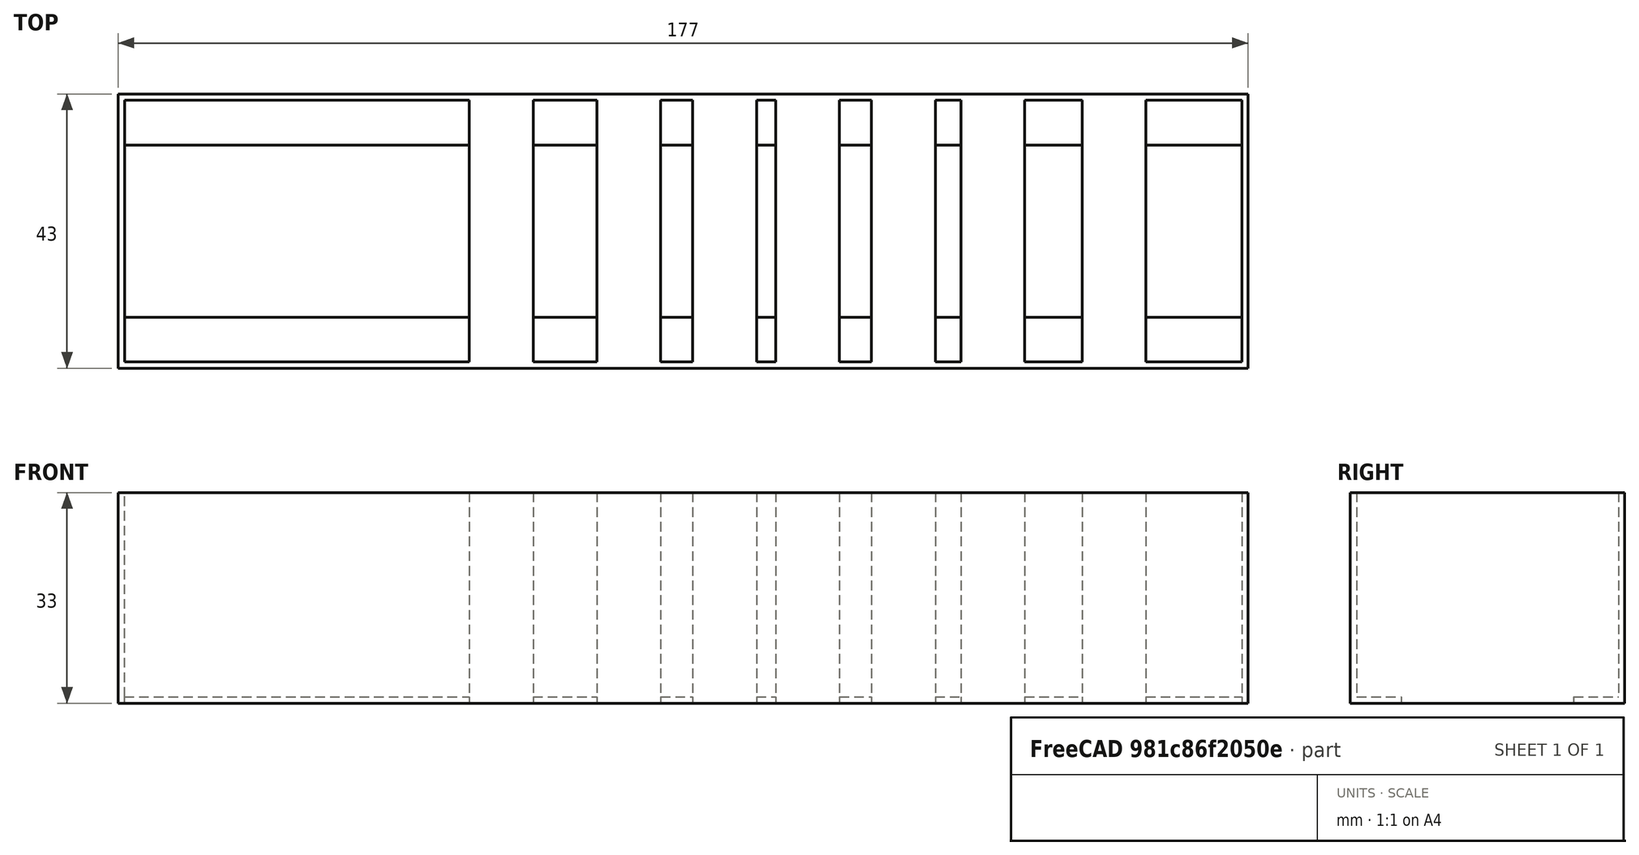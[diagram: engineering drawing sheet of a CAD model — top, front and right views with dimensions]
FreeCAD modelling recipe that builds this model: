
FCSTD DOCUMENT  (FreeCAD 0.18R4 (GitTag))
Label: common
License: All rights reserved
LicenseURL: http://en.wikipedia.org/wiki/All_rights_reserved
objects: Part::Box×13, Part::Cut×2, Part::MultiFuse×2
note: 17 computed .brp shape members not serialized (recipe doc carries the construction recipe); baked Part::Feature solids carry a one-line shape summary decoded from their .brp

FEATURE [Part::Box] Box  label="Cube"
  AttacherType = Attacher::AttachEngine3D
  Height = 33
  Length = 202
  Width = 43
FEATURE [Part::Box] Box001  label="Cube001"
  AttacherType = Attacher::AttachEngine3D
  Height = 33
  Length = 200
  Placement = pos=(1,1,0) rot=(0,0,1;0rad)
  Width = 41
FEATURE [Part::Cut] Cut
  Base = -> Box
  Tool = -> Box001
FEATURE [Part::Box] Box002  label="Cube002"
  AttacherType = Attacher::AttachEngine3D
  Height = 1
  Length = 202
  Width = 8
FEATURE [Part::Box] Box003  label="Cube003"
  AttacherType = Attacher::AttachEngine3D
  Height = 1
  Length = 202
  Placement = pos=(0,35,0) rot=(0,0,1;0rad)
  Width = 8
FEATURE [Part::MultiFuse] Fusion
  Shapes = -> [Cut,Box002,Box003]
FEATURE [Part::Box] Box004  label="Cube004"
  AttacherType = Attacher::AttachEngine3D
  Height = 33
  Length = 10
  Placement = pos=(55,0,0) rot=(0,0,1;0rad)
  Width = 43
FEATURE [Part::Box] Box005  label="Cube005"
  AttacherType = Attacher::AttachEngine3D
  Height = 33
  Length = 10
  Placement = pos=(75,0,0) rot=(0,0,1;0rad)
  Width = 43
FEATURE [Part::Box] Box006  label="Cube006"
  AttacherType = Attacher::AttachEngine3D
  Height = 33
  Length = 10
  Placement = pos=(90,0,0) rot=(0,0,1;0rad)
  Width = 43
FEATURE [Part::Box] Box007  label="Cube007"
  AttacherType = Attacher::AttachEngine3D
  Height = 33
  Length = 10
  Placement = pos=(103,0,0) rot=(0,0,1;0rad)
  Width = 43
FEATURE [Part::Box] Box008  label="Cube008"
  AttacherType = Attacher::AttachEngine3D
  Height = 33
  Length = 10
  Placement = pos=(118,0,0) rot=(0,0,1;0rad)
  Width = 43
FEATURE [Part::Box] Box009  label="Cube009"
  AttacherType = Attacher::AttachEngine3D
  Height = 33
  Length = 10
  Placement = pos=(132,0,0) rot=(0,0,1;0rad)
  Width = 43
FEATURE [Part::Box] Box010  label="Cube010"
  AttacherType = Attacher::AttachEngine3D
  Height = 33
  Length = 10
  Placement = pos=(151,0,0) rot=(0,0,1;0rad)
  Width = 43
FEATURE [Part::Box] Box011  label="Cube011"
  AttacherType = Attacher::AttachEngine3D
  Height = 33
  Length = 10
  Placement = pos=(176,0,0) rot=(0,0,1;0rad)
  Width = 43
FEATURE [Part::MultiFuse] Fusion001
  Shapes = -> [Fusion,Box010,Box011,Box005,Box007,Box004,Box006,Box008,Box009]
FEATURE [Part::Box] Box012  label="Cube012"
  AttacherType = Attacher::AttachEngine3D
  Height = 33
  Length = 25
  Placement = pos=(177,0,0) rot=(0,0,1;0rad)
  Width = 43
FEATURE [Part::Cut] Cut001
  Base = -> Fusion001
  Tool = -> Box012
